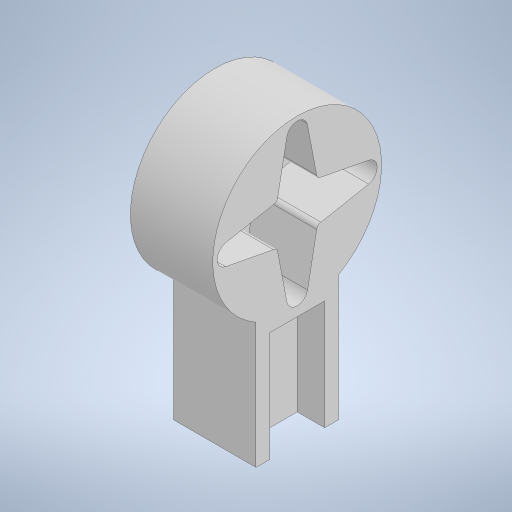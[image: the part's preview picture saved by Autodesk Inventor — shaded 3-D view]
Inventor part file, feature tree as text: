
AUTODESK INVENTOR PART (.ipt)
format: ipt  version: 2023 (Build 270158000, 158)  size: 295,936 bytes
history: native  units: in
note: dims shown in document units (in); Inventor stores cm internally (conversion verified against a paired STEP export)
features: extrude x5, sketch x4, projected_geometry x3
ambient origin geometry x8: Origin, YZ Plane, XZ Plane, XY Plane, X Axis, Y Axis, Z Axis, Center Point
bodies: Solid1 (feature_tree)
feature tree (12):
  extrude  "Extrusion1"  Depth=0.75in
  extrude  "Extrusion3"  Depth=0.5in
  extrude  "Extrusion4"  Depth=1.0in
  sketch  "Sketch5"  dims[d21=0.25in d22=0.0in d25=0.625in d26=0.0625in d27=0.0in d28=0.75in d29=0.0in d30=0.02in d31=1.0in d32=0.0in d33=0.5625in d34=0.0in]
  extrude  "Extrusion5"  Depth=0.625in TaperAngle=0.0deg
  extrude  "Extrusion6"  Depth=0.75in
  sketch  "Sketch1"  dims[d0=0.75in d1=2.0in]
  sketch  "Sketch3"  dims[d2=0.75in d3=0.0in d18=0.5in]
  projected_geometry  "Projected Loop2"
  sketch  "Sketch4"  dims[d19=0.25in d20=1.0in]
  projected_geometry  "Projected Loop3"
  projected_geometry  "Projected Loop4"
